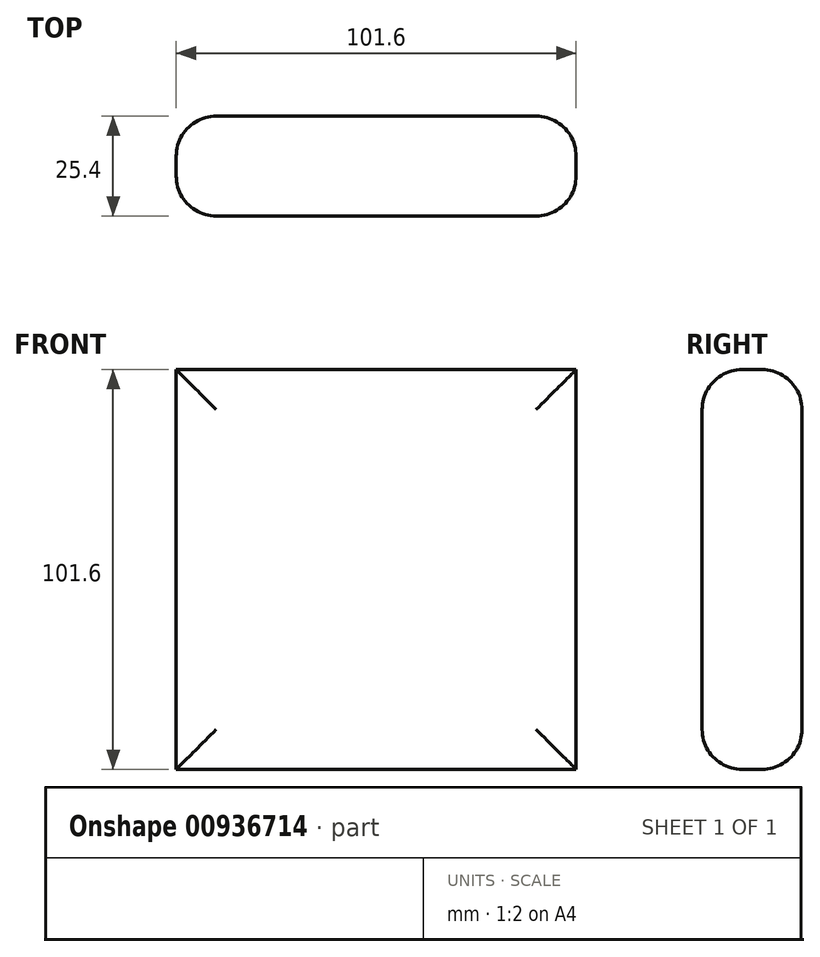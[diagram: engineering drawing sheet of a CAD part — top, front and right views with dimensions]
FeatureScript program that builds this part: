
annotation { "Feature Type Name" : "Feature", "Feature Type Description" : "" }
export const myFeature = defineFeature(function(context is Context, id is Id, definition is map)
    precondition{}
    {
        {
            var Q0;
            Q0=qCreatedBy(makeId("Front.planeOp"),FACE);
            var sketch = newSketch(context, id + "F0", { "sketchPlane" : qUnion([Q0])});
            skLineSegment(sketch, "E0.bottom", {"start": v(50.8, 50.8) * mm, "end": v(-50.8, 50.8) * mm});
            skLineSegment(sketch, "E0.top", {"start": v(50.8, -50.8) * mm, "end": v(-50.8, -50.8) * mm});
            skLineSegment(sketch, "E0.left", {"start": v(50.8, 50.8) * mm, "end": v(50.8, -50.8) * mm});
            skLineSegment(sketch, "E0.right", {"start": v(-50.8, 50.8) * mm, "end": v(-50.8, -50.8) * mm});
            skPoint(sketch, "E0.middle", {"position": v(0, 0) * mm});
            skSolve(sketch);
        }
        {
            var Q0;
            Q0 = qSketchRegion(id + "F0", true);
            extrude(context, id + "F1", {"entities" : qUnion([Q0]), "depth" : 25.4 * mm, "offsetDistance" : 25.4 * mm});
        }
        {
            var Q0;
            Q0=makeQuery(id+"F1.opExtrude","CAP_FACE",FACE,{"disambiguationData":[OSD([sQuery(id+"F0.wireOp",EDGE,"E0.bottom"),sQuery(id+"F0.wireOp",EDGE,"E0.top"),sQuery(id+"F0.wireOp",EDGE,"E0.left"),sQuery(id+"F0.wireOp",EDGE,"E0.right")])],"isStart":false});
            var Q1;
            Q1=makeQuery(id+"F1.opExtrude","CAP_FACE",FACE,{"disambiguationData":[OSD([sQuery(id+"F0.wireOp",EDGE,"E0.bottom"),sQuery(id+"F0.wireOp",EDGE,"E0.top"),sQuery(id+"F0.wireOp",EDGE,"E0.left"),sQuery(id+"F0.wireOp",EDGE,"E0.right")])],"isStart":true});
            fillet(context, id + "F2", {"entities" : qUnion([Q0, Q1]), "radius" : 10.16 * mm, "tangentPropagation" : true, "rho" : 0, "crossSection" : FilletCrossSection.CONIC, "allowEdgeOverflow" : false});
        }
    });
